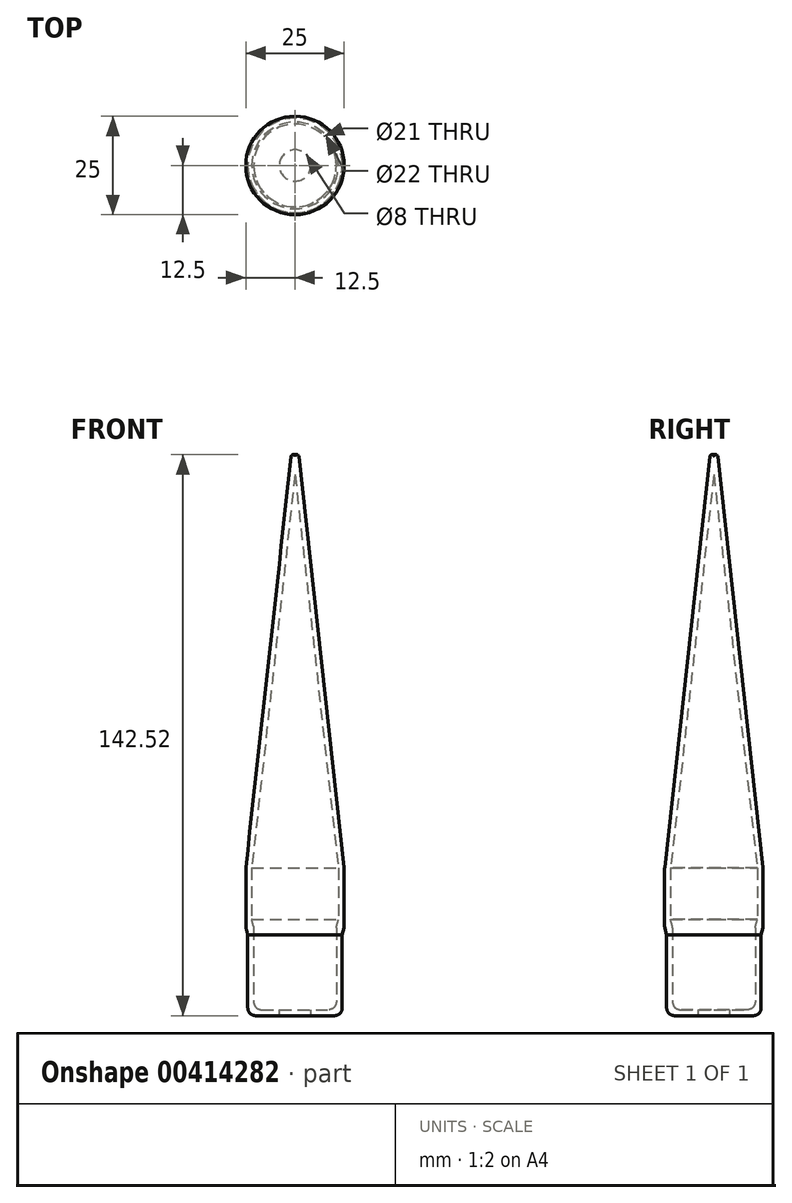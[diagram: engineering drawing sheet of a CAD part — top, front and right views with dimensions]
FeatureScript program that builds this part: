
annotation { "Feature Type Name" : "Feature", "Feature Type Description" : "" }
export const myFeature = defineFeature(function(context is Context, id is Id, definition is map)
    precondition{}
    {
        {
            var Q0;
            Q0=qCreatedBy(makeId("Front.planeOp"),FACE);
            var sketch = newSketch(context, id + "F0", { "sketchPlane" : qUnion([Q0])});
            skLineSegment(sketch, "E0", {"start": v(-12, -17) * mm, "end": v(-12, -30) * mm});
            skLineSegment(sketch, "E1", {"start": v(-10.5, -15) * mm, "end": v(-10.5, -30) * mm});
            skLineSegment(sketch, "E2", {"start": v(-12, -30) * mm, "end": v(-12, -37.5) * mm});
            skLineSegment(sketch, "E3", {"start": v(-12, -37.5) * mm, "end": v(0, -37.5) * mm});
            skLineSegment(sketch, "E4", {"start": v(0, -37.5) * mm, "end": v(0, -36) * mm});
            skLineSegment(sketch, "E5", {"start": v(0, -36) * mm, "end": v(-10.5, -36) * mm});
            skLineSegment(sketch, "E6", {"start": v(-10.5, -36) * mm, "end": v(-10.5, -30) * mm});
            skPoint(sketch, "E7", {"position": v(-12, -15) * mm});
            skPoint(sketch, "E8", {"position": v(-10.5, -15) * mm});
            skPoint(sketch, "E9.orphan", {"position": v(-10.5, 0) * mm});
            skPoint(sketch, "E10.orphan", {"position": v(-12, 0) * mm});
            skLineSegment(sketch, "E11", {"start": v(-12.5, 0) * mm, "end": v(-12.5, -15) * mm});
            skLineSegment(sketch, "E12", {"start": v(-11, 0) * mm, "end": v(-11, -13) * mm});
            skLineSegment(sketch, "E13", {"start": v(-12.5, 0) * mm, "end": v(-1, 104.57) * mm});
            skLineSegment(sketch, "E14", {"start": v(-11, 0) * mm, "end": v(0, 100) * mm});
            skLineSegment(sketch, "E15", {"start": v(0, 100) * mm, "end": v(-1.5, 100) * mm, "construction": true});
            skLineSegment(sketch, "E16", {"start": v(0, 100) * mm, "end": v(0, 104.52) * mm});
            skPoint(sketch, "E17.visualSharp", {"position": v(0, 113.64) * mm});
            skArc(sketch, "E17.filletArc", {"start": v(0, 104.52) * mm, "mid": v(-0.47, 105.02) * mm, "end": v(-1, 104.57) * mm});
            skLineSegment(sketch, "E18", {"start": v(-10.5, -15) * mm, "end": v(-11, -13) * mm});
            skLineSegment(sketch, "E19", {"start": v(-12.5, -15) * mm, "end": v(-12, -17) * mm});
            skPoint(sketch, "E20.trimOffspring.start.orphan", {"position": v(-11, -15) * mm});
            skSolve(sketch);
        }
        {
            var Q0;
            Q0=qCreatedBy(makeId("Top.planeOp"),FACE);
            var sketch = newSketch(context, id + "F1", { "sketchPlane" : qUnion([Q0])});
            skCircle(sketch, "E21", {"center": v(0, 0) * mm, "radius": 2.5 * mm});
            skSolve(sketch);
        }
        {
            var Q0;
            Q0=makeQuery(id+"F0.imprint","IMPRINT",FACE,{"disambiguationData":[TD([[makeQuery(id+"F0.imprint","IMPRINT",EDGE,{"derivedFrom":sQuery(id+"F0.wireOp",EDGE,"E0")}),1.0]])]});
            var Q1;
            Q1=sQuery(id+"F1.wireOp",EDGE,"E21");
            revolve(context, id + "F2", {"entities" : qUnion([Q0]), "axis" : qUnion([Q1]), "revolveType" : RevolveType.FULL});
        }
        {
            var Q0;
            Q0=makeQuery(id+"F2.opRevolve","SWEPT_FACE",FACE,{"disambiguationData":[OSD([sQuery(id+"F0.wireOp",EDGE,"E3")])]});
            var sketch = newSketch(context, id + "F3", { "sketchPlane" : qUnion([Q0])});
            skCircle(sketch, "E22", {"center": v(0, 0) * mm, "radius": 4 * mm});
            skSolve(sketch);
        }
        {
            var Q0;
            Q0=makeQuery(id+"F3.imprint","IMPRINT",FACE,{"disambiguationData":[TD([[makeQuery(id+"F3.imprint","IMPRINT",EDGE,{"derivedFrom":sQuery(id+"F3.wireOp",EDGE,"E22")}),1.0]])]});
            var Q1;
            {var subQ0=sQuery(id+"F0.wireOp",EDGE,"E3");Q1=makeQuery(id+"F3.imprint","IMPRINT",FACE,{"disambiguationData":[TD([[makeQuery(id+"F3.imprint","IMPRINT",EDGE,{"derivedFrom":makeQuery(id+"F5.opFillet","BLEND_EDGE",EDGE,{"blendedFrom":[makeQuery(id+"F2.opRevolve","SWEPT_EDGE",EDGE,{"disambiguationData":[OSD([sQuery(id+"F0.wireOp",EDGE,"E2"),subQ0])]}),makeQuery(id+"F2.opRevolve","SWEPT_FACE",FACE,{"disambiguationData":[OSD([subQ0])]})],"blendedInto":[makeQuery(id+"F2.opRevolve","SWEPT_FACE",FACE,{"disambiguationData":[OSD([subQ0])]})]})}),1.0]])]});}
            extrude(context, id + "F4", {"entities" : qUnion([Q0, Q1]), "operationType" : NewBodyOperationType.REMOVE, "oppositeDirection" : true, "depth" : 25 * mm});
        }
        {
            var Q0;
            Q0=makeQuery(id+"F2.opRevolve","SWEPT_EDGE",EDGE,{"disambiguationData":[OSD([sQuery(id+"F0.wireOp",EDGE,"E11"),sQuery(id+"F0.wireOp",EDGE,"wWiemt9r-7ztU-drZh-PdV8-ENJEC7tMP3Fv")])]});
            var Q1;
            Q1=makeQuery(id+"F2.opRevolve","SWEPT_EDGE",EDGE,{"disambiguationData":[OSD([sQuery(id+"F0.wireOp",EDGE,"E11"),sQuery(id+"F0.wireOp",EDGE,"E13")])]});
            var Q2;
            Q2=makeQuery(id+"F2.opRevolve","SWEPT_EDGE",EDGE,{"disambiguationData":[OSD([sQuery(id+"F0.wireOp",EDGE,"E2"),sQuery(id+"F0.wireOp",EDGE,"E3")])]});
            var Q3;
            Q3=makeQuery(id+"F2.opRevolve","SWEPT_FACE",FACE,{"disambiguationData":[OSD([sQuery(id+"F0.wireOp",EDGE,"E1"),sQuery(id+"F0.wireOp",EDGE,"E6")])]});
            fillet(context, id + "F5", {"entities" : qUnion([Q0, Q1, Q2, Q3]), "radius" : 2 * mm, "tangentPropagation" : true, "allowEdgeOverflow" : false});
        }
    });
